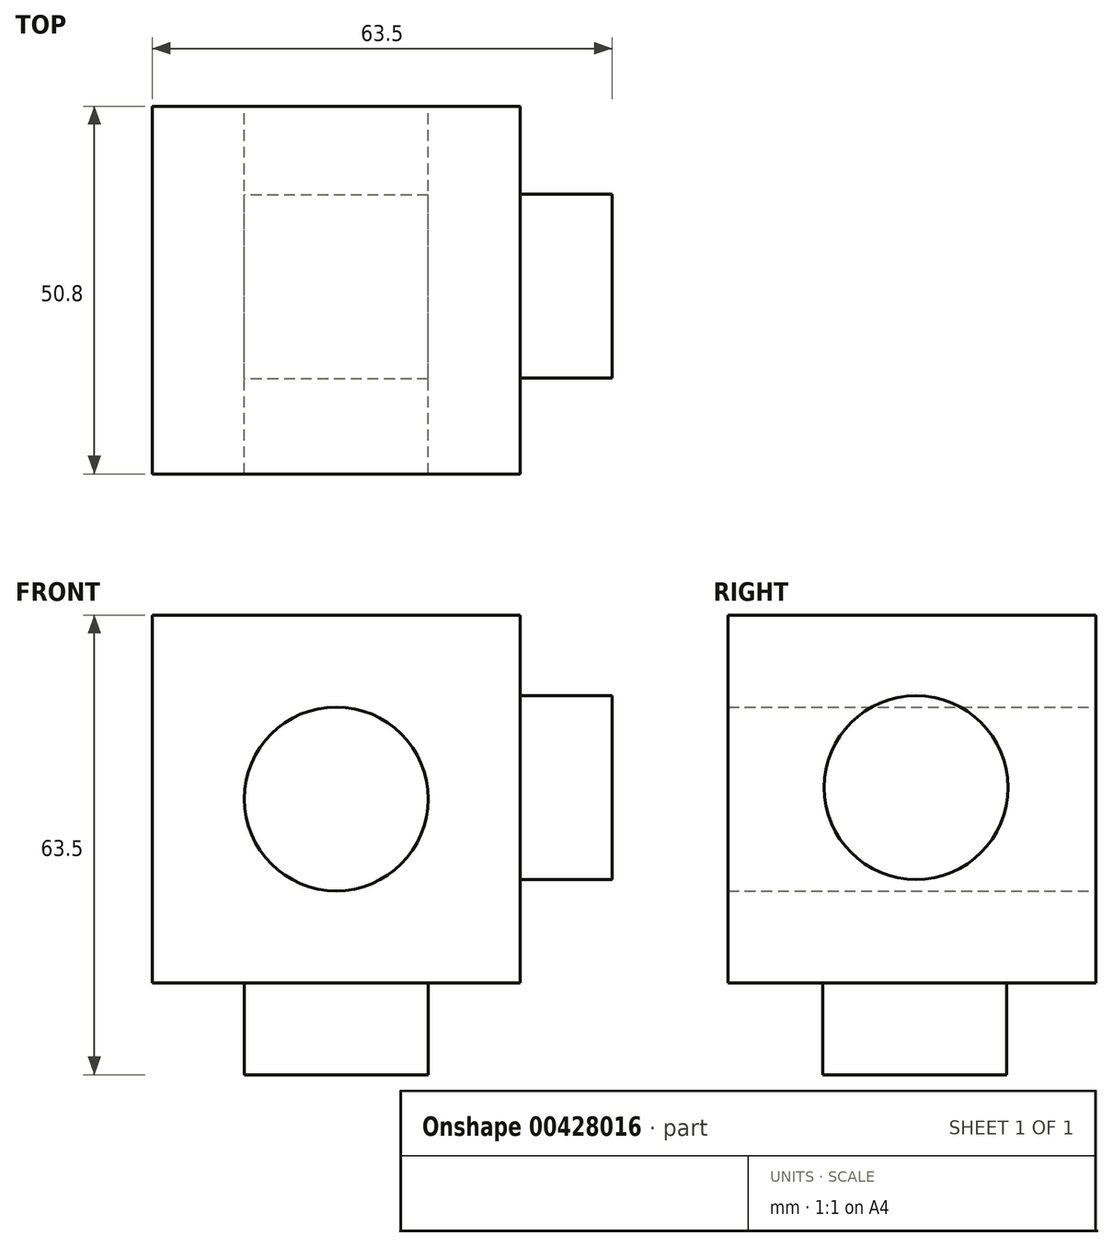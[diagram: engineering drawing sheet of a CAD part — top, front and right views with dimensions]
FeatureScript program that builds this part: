
annotation { "Feature Type Name" : "Feature", "Feature Type Description" : "" }
export const myFeature = defineFeature(function(context is Context, id is Id, definition is map)
    precondition{}
    {
        {
            var Q0;
            Q0=qCreatedBy(makeId("Front.planeOp"),FACE);
            var sketch = newSketch(context, id + "F0", { "sketchPlane" : qUnion([Q0])});
            skLineSegment(sketch, "E0.bottom", {"start": v(0, 0) * mm, "end": v(-50.8, 0) * mm});
            skLineSegment(sketch, "E0.top", {"start": v(0, 50.8) * mm, "end": v(-50.8, 50.8) * mm});
            skLineSegment(sketch, "E0.left", {"start": v(0, 0) * mm, "end": v(0, 50.8) * mm});
            skLineSegment(sketch, "E0.right", {"start": v(-50.8, 0) * mm, "end": v(-50.8, 50.8) * mm});
            skCircle(sketch, "E1", {"center": v(-25.4, 25.4) * mm, "radius": 12.7 * mm});
            skPoint(sketch, "E2.start.orphan", {"position": v(-25.4, 50.8) * mm});
            skPoint(sketch, "E3.start.orphan", {"position": v(0, 25.4) * mm});
            skPoint(sketch, "E4.start.orphan", {"position": v(-50.8, 25.4) * mm});
            skPoint(sketch, "E5.start.orphan", {"position": v(-25.4, 0) * mm});
            skSolve(sketch);
        }
        {
            var Q0;
            Q0 = qSketchRegion(id + "F0", true);
            extrude(context, id + "F1", {"entities" : qUnion([Q0]), "depth" : 50.8 * mm});
        }
        {
            var Q0;
            Q0=qCreatedBy(makeId("Right.planeOp"),FACE);
            var sketch = newSketch(context, id + "F2", { "sketchPlane" : qUnion([Q0])});
            skCircle(sketch, "E6", {"center": v(-24.83, 26.97) * mm, "radius": 12.7 * mm});
            skSolve(sketch);
        }
        {
            var Q0;
            Q0=makeQuery(id+"F2.imprint","IMPRINT",FACE,{"disambiguationData":[TD([[makeQuery(id+"F2.imprint","IMPRINT",EDGE,{"derivedFrom":sQuery(id+"F2.wireOp",EDGE,"E6")}),1.0]])]});
            extrude(context, id + "F3", {"entities" : qUnion([Q0]), "operationType" : NewBodyOperationType.ADD, "depth" : 12.7 * mm});
        }
        {
            var Q0;
            Q0=qCreatedBy(makeId("Top.planeOp"),FACE);
            var sketch = newSketch(context, id + "F4", { "sketchPlane" : qUnion([Q0])});
            skLineSegment(sketch, "E7", {"start": v(0, -25.4) * mm, "end": v(0, -50.8) * mm});
            skLineSegment(sketch, "E8", {"start": v(-12.7, -25.4) * mm, "end": v(-12.7, -25.4) * mm});
            skPoint(sketch, "E9.end.orphan", {"position": v(-25.4, -25.4) * mm});
            skPoint(sketch, "E10.oppositeSnap0", {"position": v(-6.35, -25.4) * mm});
            skPoint(sketch, "E10.right.end.orphan", {"position": v(-48.64, -25.4) * mm});
            skLineSegment(sketch, "E11.bottom", {"start": v(-12.7, -37.7) * mm, "end": v(-38.1, -37.7) * mm});
            skLineSegment(sketch, "E11.top", {"start": v(-12.7, -12.3) * mm, "end": v(-38.1, -12.3) * mm});
            skLineSegment(sketch, "E11.left", {"start": v(-12.7, -37.7) * mm, "end": v(-12.7, -12.3) * mm});
            skLineSegment(sketch, "E11.right", {"start": v(-38.1, -37.7) * mm, "end": v(-38.1, -12.3) * mm});
            skPoint(sketch, "E12.end.orphan", {"position": v(-25.4, 0) * mm});
            skPoint(sketch, "E12.start.orphan", {"position": v(-25.8, -12.3) * mm});
            skPoint(sketch, "E13.end.orphan", {"position": v(-25.4, -50.8) * mm});
            skPoint(sketch, "E14.orphan", {"position": v(0, 0) * mm});
            skSolve(sketch);
        }
        {
            var Q0;
            Q0=makeQuery(id+"F4.imprint","IMPRINT",FACE,{"disambiguationData":[TD([[makeQuery(id+"F4.imprint","IMPRINT",EDGE,{"derivedFrom":sQuery(id+"F4.wireOp",EDGE,"E11.bottom")}),-1.0]])]});
            extrude(context, id + "F5", {"entities" : qUnion([Q0]), "operationType" : NewBodyOperationType.ADD, "oppositeDirection" : true, "depth" : 12.7 * mm});
        }
    });
